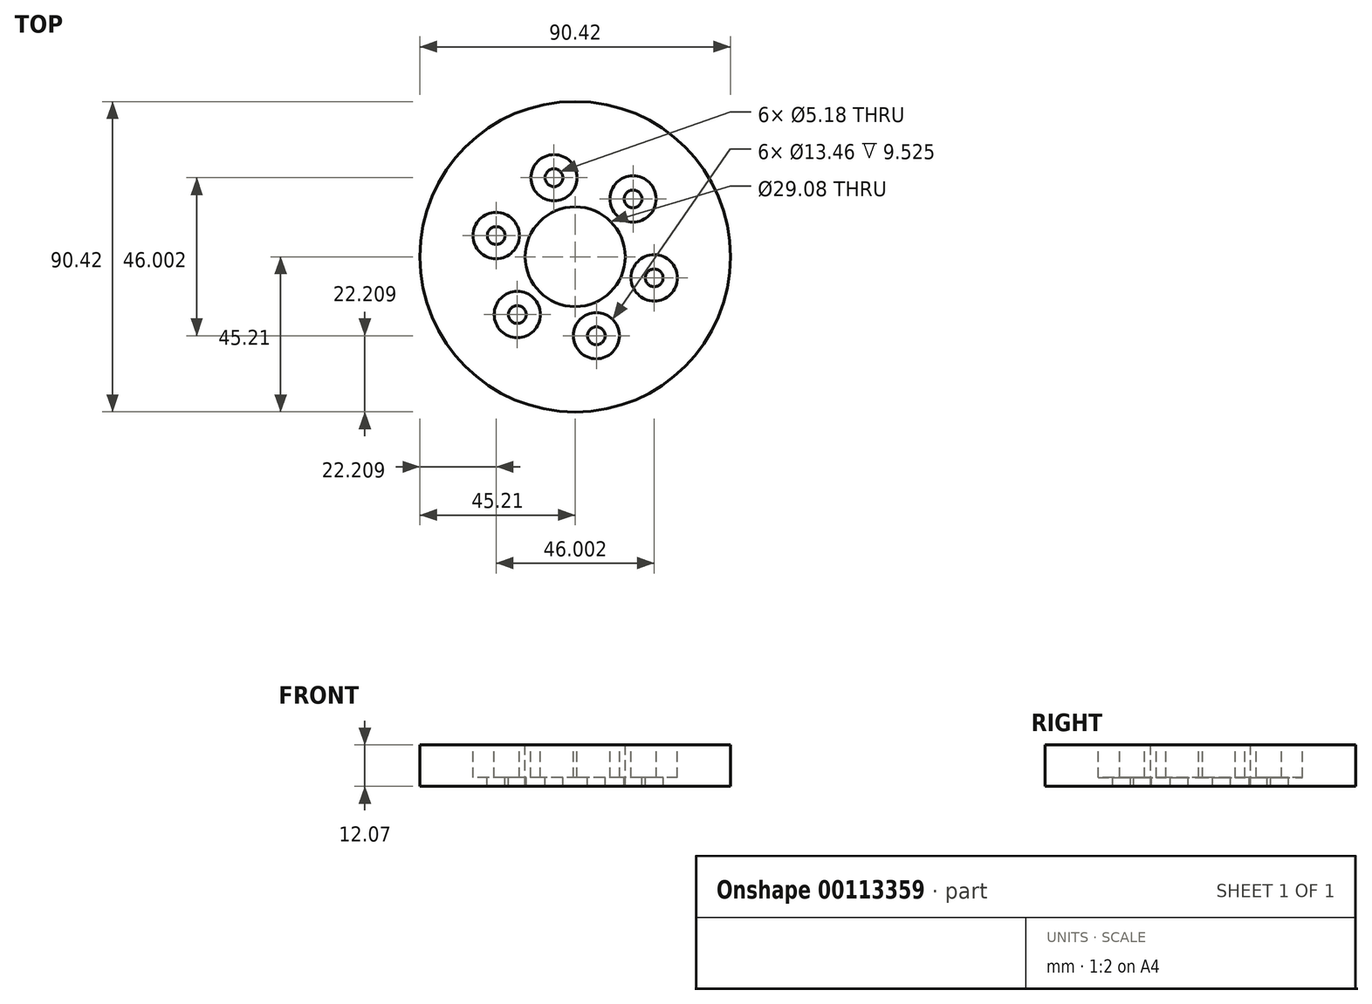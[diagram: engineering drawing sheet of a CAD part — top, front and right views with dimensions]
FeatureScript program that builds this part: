
annotation { "Feature Type Name" : "Feature", "Feature Type Description" : "" }
export const myFeature = defineFeature(function(context is Context, id is Id, definition is map)
    precondition{}
    {
        {
            var Q0;
            Q0=qCreatedBy(makeId("Top.planeOp"),FACE);
            var sketch = newSketch(context, id + "F0", { "sketchPlane" : qUnion([Q0])});
            skCircle(sketch, "E0", {"center": v(0, 0) * mm, "radius": 45.21 * mm});
            skSolve(sketch);
        }
        {
            var Q0;
            Q0=qSketchRegion(id+"F0",true);
            extrude(context, id + "F1", {"entities" : qUnion([Q0]), "depth" : 12.06 * mm, "offsetDistance" : 25.4 * mm});
        }
        {
            var Q0;
            Q0=makeQuery(id+"F1.opExtrude","CAP_FACE",FACE,{"disambiguationData":[OSD([sQuery(id+"F0.wireOp",EDGE,"E0")])],"isStart":false});
            var sketch = newSketch(context, id + "F2", { "sketchPlane" : qUnion([Q0])});
            skLineSegment(sketch, "E1", {"start": v(0, 0) * mm, "end": v(0, 60.06) * mm, "construction": true});
            skLineSegment(sketch, "E2", {"start": v(0, 0) * mm, "end": v(-13.99, 52.2) * mm, "construction": true});
            skCircle(sketch, "E3", {"center": v(0, 0) * mm, "radius": 23.81 * mm, "construction": true});
            skCircle(sketch, "E4", {"center": v(-6.16, 23) * mm, "radius": 2.6 * mm});
            skCircle(sketch, "E5.1.0", {"center": v(-23, 6.16) * mm, "radius": 2.6 * mm});
            skCircle(sketch, "E5.2.0", {"center": v(-16.84, -16.84) * mm, "radius": 2.6 * mm});
            skCircle(sketch, "E6.1.3.0", {"center": v(6.16, -23) * mm, "radius": 2.6 * mm});
            skCircle(sketch, "E6.1.4.0", {"center": v(23, -6.16) * mm, "radius": 2.6 * mm});
            skCircle(sketch, "E6.1.5.0", {"center": v(16.84, 16.84) * mm, "radius": 2.6 * mm});
            skLineSegment(sketch, "E7", {"start": v(0, 0) * mm, "end": v(16.84, 16.84) * mm, "construction": true});
            skSolve(sketch);
        }
        {
            var Q0;
            Q0=makeQuery(id+"F2.imprint","IMPRINT",FACE,{"disambiguationData":[TD([[makeQuery(id+"F2.imprint","IMPRINT",EDGE,{"derivedFrom":sQuery(id+"F2.wireOp",EDGE,"E4")}),1.0]])]});
            var Q1;
            Q1=makeQuery(id+"F2.imprint","IMPRINT",FACE,{"disambiguationData":[TD([[makeQuery(id+"F2.imprint","IMPRINT",EDGE,{"derivedFrom":sQuery(id+"F2.wireOp",EDGE,"E5.1.0")}),1.0]])]});
            var Q2;
            Q2=makeQuery(id+"F2.imprint","IMPRINT",FACE,{"disambiguationData":[TD([[makeQuery(id+"F2.imprint","IMPRINT",EDGE,{"derivedFrom":sQuery(id+"F2.wireOp",EDGE,"E5.2.0")}),1.0]])]});
            var Q3;
            Q3=makeQuery(id+"F2.imprint","IMPRINT",FACE,{"disambiguationData":[TD([[makeQuery(id+"F2.imprint","IMPRINT",EDGE,{"derivedFrom":sQuery(id+"F2.wireOp",EDGE,"E6.1.3.0")}),1.0]])]});
            var Q4;
            Q4=makeQuery(id+"F2.imprint","IMPRINT",FACE,{"disambiguationData":[TD([[makeQuery(id+"F2.imprint","IMPRINT",EDGE,{"derivedFrom":sQuery(id+"F2.wireOp",EDGE,"E6.1.4.0")}),1.0]])]});
            var Q5;
            Q5=makeQuery(id+"F2.imprint","IMPRINT",FACE,{"disambiguationData":[TD([[makeQuery(id+"F2.imprint","IMPRINT",EDGE,{"derivedFrom":sQuery(id+"F2.wireOp",EDGE,"E6.1.5.0")}),1.0]])]});
            extrude(context, id + "F3", {"entities" : qUnion([Q0, Q1, Q2, Q3, Q4, Q5]), "operationType" : NewBodyOperationType.REMOVE, "oppositeDirection" : true, "depth" : 25.4 * mm});
        }
        {
            var Q0;
            Q0=makeQuery(id+"F2.imprint","IMPRINT",FACE,{"disambiguationData":[TD([[makeQuery(id+"F2.imprint","IMPRINT",EDGE,{"derivedFrom":sQuery(id+"F2.wireOp",EDGE,"E4")}),-1.0]])]});
            var sketch = newSketch(context, id + "F4", { "sketchPlane" : qUnion([Q0])});
            skCircle(sketch, "E8", {"center": v(0, 0) * mm, "radius": 14.54 * mm});
            skSolve(sketch);
        }
        {
            var Q0;
            Q0=qSketchRegion(id+"F4",true);
            extrude(context, id + "F5", {"entities" : qUnion([Q0]), "operationType" : NewBodyOperationType.REMOVE, "oppositeDirection" : true, "depth" : 25.4 * mm});
        }
        {
            var Q0;
            Q0=makeQuery(id+"F2.imprint","IMPRINT",FACE,{"disambiguationData":[TD([[makeQuery(id+"F2.imprint","IMPRINT",EDGE,{"derivedFrom":sQuery(id+"F2.wireOp",EDGE,"E4")}),-1.0]])]});
            var sketch = newSketch(context, id + "F6", { "sketchPlane" : qUnion([Q0])});
            skCircle(sketch, "E9", {"center": v(-6.16, 23) * mm, "radius": 6.73 * mm});
            skCircle(sketch, "E10", {"center": v(16.84, 16.84) * mm, "radius": 6.73 * mm});
            skCircle(sketch, "E11", {"center": v(23, -6.16) * mm, "radius": 6.73 * mm});
            skCircle(sketch, "E12", {"center": v(6.16, -23) * mm, "radius": 6.73 * mm});
            skCircle(sketch, "E13", {"center": v(-16.84, -16.84) * mm, "radius": 6.73 * mm});
            skCircle(sketch, "E14", {"center": v(-23, 6.16) * mm, "radius": 6.73 * mm});
            skSolve(sketch);
        }
        {
            var Q0;
            Q0=qSketchRegion(id+"F6",true);
            extrude(context, id + "F7", {"entities" : qUnion([Q0]), "operationType" : NewBodyOperationType.REMOVE, "oppositeDirection" : true, "depth" : 9.52 * mm, "offsetDistance" : 25.4 * mm});
        }
    });
